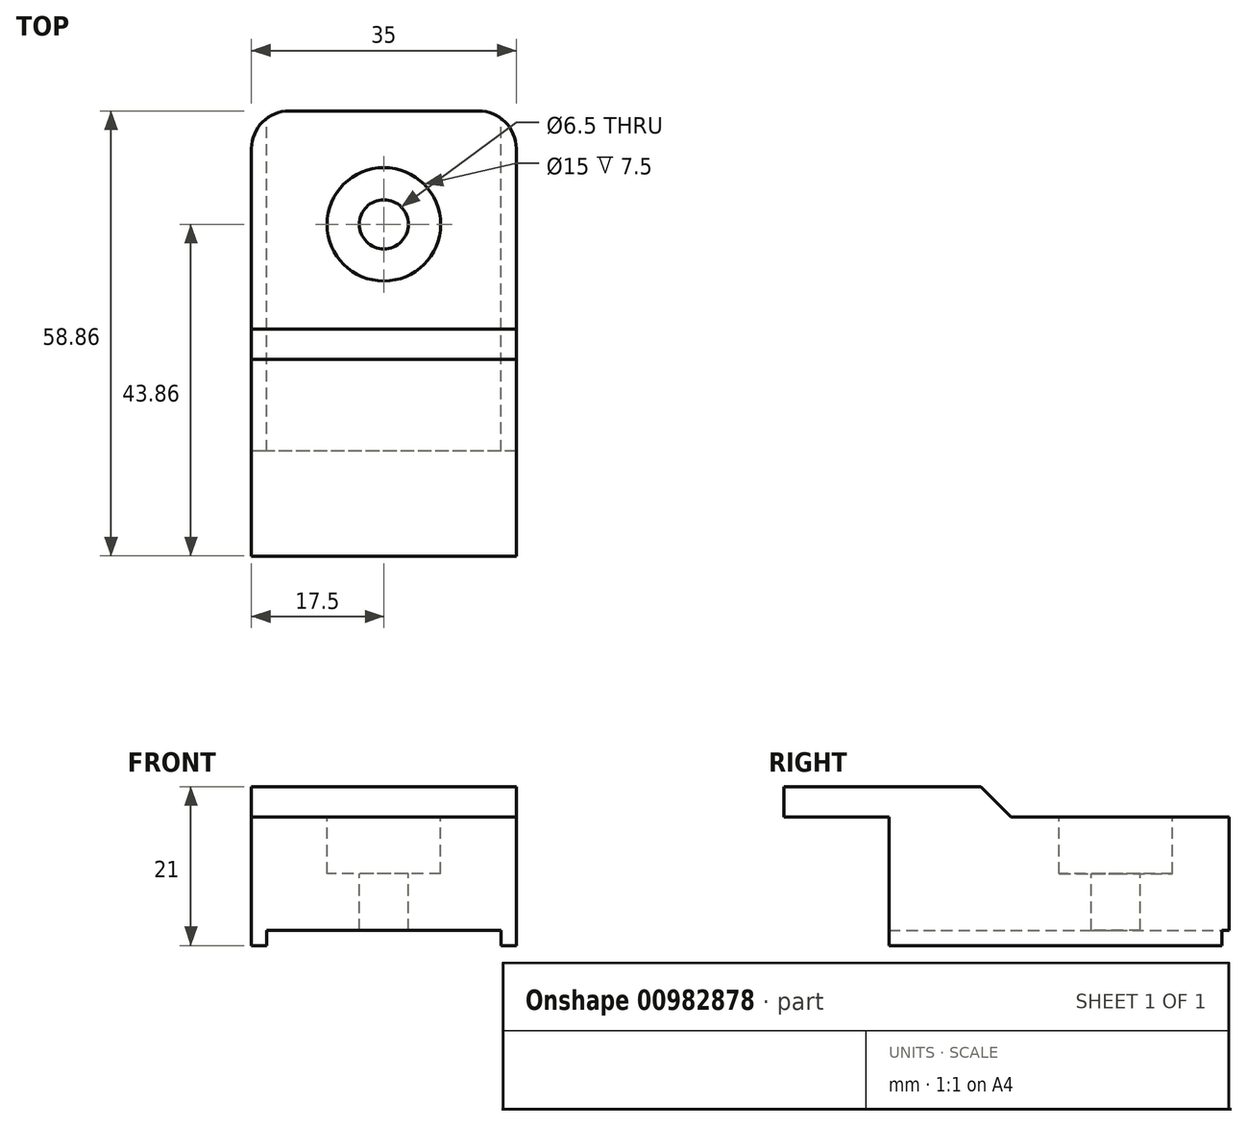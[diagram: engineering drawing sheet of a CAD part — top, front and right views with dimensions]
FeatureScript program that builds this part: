
annotation { "Feature Type Name" : "Feature", "Feature Type Description" : "" }
export const myFeature = defineFeature(function(context is Context, id is Id, definition is map)
    precondition{}
    {
        {
            var Q0;
            Q0=qCreatedBy(makeId("Top.planeOp"),FACE);
            var sketch = newSketch(context, id + "F0", { "sketchPlane" : qUnion([Q0])});
            skLineSegment(sketch, "E0.bottom", {"start": v(17.5, 22.5) * mm, "end": v(-17.5, 22.5) * mm});
            skLineSegment(sketch, "E0.top", {"start": v(17.5, -22.5) * mm, "end": v(-17.5, -22.5) * mm});
            skLineSegment(sketch, "E0.left", {"start": v(17.5, 22.5) * mm, "end": v(17.5, -22.5) * mm});
            skLineSegment(sketch, "E0.right", {"start": v(-17.5, 22.5) * mm, "end": v(-17.5, -22.5) * mm});
            skPoint(sketch, "E0.middle", {"position": v(0, 0) * mm});
            skSolve(sketch);
        }
        {
            var Q0;
            Q0 = qSketchRegion(id + "F0", true);
            extrude(context, id + "F1", {"entities" : qUnion([Q0]), "depth" : 15 * mm, "offsetDistance" : 25 * mm});
        }
        {
            var Q0;
            Q0=makeQuery(id+"F1.opExtrude","CAP_FACE",FACE,{"disambiguationData":[OSD([sQuery(id+"F0.wireOp",EDGE,"E0.bottom"),sQuery(id+"F0.wireOp",EDGE,"E0.top"),sQuery(id+"F0.wireOp",EDGE,"E0.left"),sQuery(id+"F0.wireOp",EDGE,"E0.right")])],"isStart":true});
            var sketch = newSketch(context, id + "F2", { "sketchPlane" : qUnion([Q0])});
            skLineSegment(sketch, "E1.bottom", {"start": v(-17.5, 22.5) * mm, "end": v(-15.5, 22.5) * mm});
            skLineSegment(sketch, "E1.top", {"start": v(-17.5, -22.5) * mm, "end": v(-15.5, -22.5) * mm});
            skLineSegment(sketch, "E1.left", {"start": v(-17.5, 22.5) * mm, "end": v(-17.5, -22.5) * mm});
            skLineSegment(sketch, "E1.right", {"start": v(-15.5, 22.5) * mm, "end": v(-15.5, -22.5) * mm});
            skLineSegment(sketch, "E2.bottom", {"start": v(17.5, 22.5) * mm, "end": v(15.5, 22.5) * mm});
            skLineSegment(sketch, "E2.top", {"start": v(17.5, -22.5) * mm, "end": v(15.5, -22.5) * mm});
            skLineSegment(sketch, "E2.left", {"start": v(17.5, 22.5) * mm, "end": v(17.5, -22.5) * mm});
            skLineSegment(sketch, "E2.right", {"start": v(15.5, 22.5) * mm, "end": v(15.5, -22.5) * mm});
            skSolve(sketch);
        }
        {
            var Q0;
            Q0=makeQuery(id+"F2.imprint","IMPRINT",FACE,{"disambiguationData":[TD([[makeQuery(id+"F2.imprint","IMPRINT",EDGE,{"derivedFrom":sQuery(id+"F2.wireOp",EDGE,"E1.bottom")}),1.0]])]});
            var Q1;
            Q1=makeQuery(id+"F2.imprint","IMPRINT",FACE,{"disambiguationData":[TD([[makeQuery(id+"F2.imprint","IMPRINT",EDGE,{"derivedFrom":sQuery(id+"F2.wireOp",EDGE,"E2.bottom")}),1.0]])]});
            extrude(context, id + "F3", {"entities" : qUnion([Q0, Q1]), "operationType" : NewBodyOperationType.ADD, "depth" : 2 * mm, "offsetDistance" : 25 * mm});
        }
        {
            var Q0;
            Q0=makeQuery(id+"F1.opExtrude","CAP_FACE",FACE,{"disambiguationData":[OSD([sQuery(id+"F0.wireOp",EDGE,"E0.bottom"),sQuery(id+"F0.wireOp",EDGE,"E0.top"),sQuery(id+"F0.wireOp",EDGE,"E0.left"),sQuery(id+"F0.wireOp",EDGE,"E0.right")])],"isStart":false});
            var sketch = newSketch(context, id + "F4", { "sketchPlane" : qUnion([Q0])});
            skLineSegment(sketch, "E3.bottom", {"start": v(-17.5, -6.36) * mm, "end": v(17.5, -6.36) * mm});
            skLineSegment(sketch, "E3.top", {"start": v(-17.5, -36.36) * mm, "end": v(17.5, -36.36) * mm});
            skLineSegment(sketch, "E3.left", {"start": v(-17.5, -6.36) * mm, "end": v(-17.5, -36.36) * mm});
            skLineSegment(sketch, "E3.right", {"start": v(17.5, -6.36) * mm, "end": v(17.5, -36.36) * mm});
            skSolve(sketch);
        }
        {
            var Q0;
            {var subQ0=sQuery(id+"F4.wireOp",EDGE,"E3.top");Q0=makeQuery(id+"F4.imprint","IMPRINT",FACE,{"disambiguationData":[TD([[makeQuery(id+"F4.imprint","IMPRINT",EDGE,{"derivedFrom":subQ0}),1.0]])]});}
            var Q1;
            {var subQ0=sQuery(id+"F4.wireOp",EDGE,"E3.bottom");Q1=makeQuery(id+"F4.imprint","IMPRINT",FACE,{"disambiguationData":[TD([[makeQuery(id+"F4.imprint","IMPRINT",EDGE,{"derivedFrom":subQ0}),-1.0]])]});}
            extrude(context, id + "F5", {"entities" : qUnion([Q0, Q1]), "operationType" : NewBodyOperationType.ADD, "depth" : 4 * mm, "offsetDistance" : 25 * mm});
        }
        {
            var Q0;
            Q0=makeQuery(id+"F5.opExtrude","CAP_EDGE",EDGE,{"disambiguationData":[OSD([sQuery(id+"F4.wireOp",EDGE,"E3.bottom")])],"isStart":false});
            chamfer(context, id + "F6", {"entities" : qUnion([Q0]), "width" : 4 * mm, "tangentPropagation" : true});
        }
        {
            var Q0;
            Q0=makeQuery(id+"F1.opExtrude","CAP_FACE",FACE,{"disambiguationData":[OSD([sQuery(id+"F0.wireOp",EDGE,"E0.bottom"),sQuery(id+"F0.wireOp",EDGE,"E0.top"),sQuery(id+"F0.wireOp",EDGE,"E0.left"),sQuery(id+"F0.wireOp",EDGE,"E0.right")])],"isStart":false});
            var sketch = newSketch(context, id + "F7", { "sketchPlane" : qUnion([Q0])});
            skCircle(sketch, "E4", {"center": v(0, 7.5) * mm, "radius": 3.25 * mm});
            skSolve(sketch);
        }
        {
            var Q0;
            Q0=makeQuery(id+"F7.imprint","IMPRINT",FACE,{"disambiguationData":[TD([[makeQuery(id+"F7.imprint","IMPRINT",EDGE,{"derivedFrom":sQuery(id+"F7.wireOp",EDGE,"E4")}),1.0]])]});
            var Q1;
            Q1=makeQuery(id+"F1.opExtrude","CAP_FACE",FACE,{"disambiguationData":[OSD([sQuery(id+"F0.wireOp",EDGE,"E0.bottom"),sQuery(id+"F0.wireOp",EDGE,"E0.top"),sQuery(id+"F0.wireOp",EDGE,"E0.left"),sQuery(id+"F0.wireOp",EDGE,"E0.right")])],"isStart":true});
            extrude(context, id + "F8", {"entities" : qUnion([Q0]), "operationType" : NewBodyOperationType.REMOVE, "endBound" : BoundingType.UP_TO_SURFACE, "oppositeDirection" : true, "depth" : 25 * mm, "endBoundEntityFace" : qUnion([Q1]), "offsetDistance" : 25 * mm});
        }
        {
            var Q0;
            Q0=makeQuery(id+"F3.boolean.opBoolean","MERGE",EDGE,{"derivedFrom":[makeQuery(id+"F1.opExtrude","SWEPT_EDGE",EDGE,{"disambiguationData":[OSD([sQuery(id+"F0.wireOp",EDGE,"E0.bottom"),sQuery(id+"F0.wireOp",EDGE,"E0.right")])]}),makeQuery(id+"F3.opExtrude","SWEPT_EDGE",EDGE,{"disambiguationData":[OSD([sQuery(id+"F2.wireOp",EDGE,"E1.top"),sQuery(id+"F2.wireOp",EDGE,"E1.left")])]})]});
            var Q1;
            Q1=makeQuery(id+"F3.boolean.opBoolean","MERGE",EDGE,{"derivedFrom":[makeQuery(id+"F1.opExtrude","SWEPT_EDGE",EDGE,{"disambiguationData":[OSD([sQuery(id+"F0.wireOp",EDGE,"E0.bottom"),sQuery(id+"F0.wireOp",EDGE,"E0.left")])]}),makeQuery(id+"F3.opExtrude","SWEPT_EDGE",EDGE,{"disambiguationData":[OSD([sQuery(id+"F2.wireOp",EDGE,"E2.top"),sQuery(id+"F2.wireOp",EDGE,"E2.left")])]})]});
            fillet(context, id + "F9", {"entities" : qUnion([Q0, Q1]), "radius" : 5 * mm, "tangentPropagation" : true, "allowEdgeOverflow" : false});
        }
        {
            var Q0;
            Q0=makeQuery(id+"F1.opExtrude","CAP_FACE",FACE,{"disambiguationData":[OSD([sQuery(id+"F0.wireOp",EDGE,"E0.bottom"),sQuery(id+"F0.wireOp",EDGE,"E0.top"),sQuery(id+"F0.wireOp",EDGE,"E0.left"),sQuery(id+"F0.wireOp",EDGE,"E0.right")])],"isStart":false});
            var sketch = newSketch(context, id + "F10", { "sketchPlane" : qUnion([Q0])});
            skCircle(sketch, "E5", {"center": v(0, 7.5) * mm, "radius": 7.5 * mm});
            skSolve(sketch);
        }
        {
            var Q0;
            Q0=makeQuery(id+"F10.imprint","IMPRINT",FACE,{"disambiguationData":[TD([[makeQuery(id+"F10.imprint","IMPRINT",EDGE,{"derivedFrom":sQuery(id+"F10.wireOp",EDGE,"E5")}),1.0]])]});
            extrude(context, id + "F11", {"entities" : qUnion([Q0]), "operationType" : NewBodyOperationType.REMOVE, "oppositeDirection" : true, "depth" : 7.5 * mm, "offsetDistance" : 25 * mm});
        }
    });
